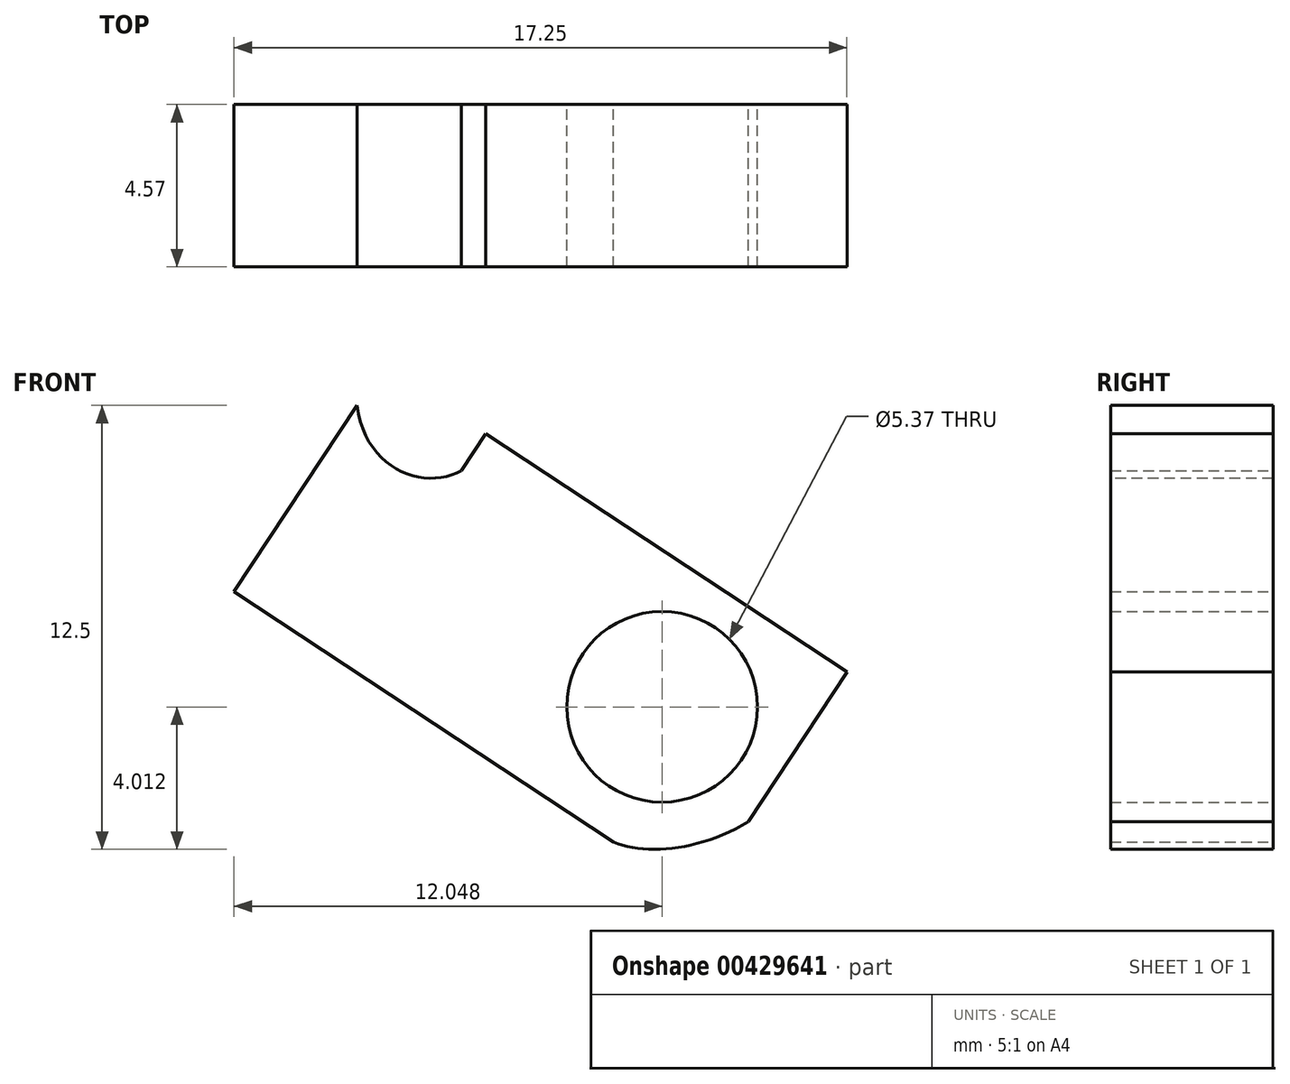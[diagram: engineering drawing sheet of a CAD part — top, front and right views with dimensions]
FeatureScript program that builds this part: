
annotation { "Feature Type Name" : "Feature", "Feature Type Description" : "" }
export const myFeature = defineFeature(function(context is Context, id is Id, definition is map)
    precondition{}
    {
        {
            var Q0;
            Q0=qCreatedBy(makeId("Front.planeOp"),FACE);
            var sketch = newSketch(context, id + "F0", { "sketchPlane" : qUnion([Q0])});
            skPoint(sketch, "E0.startSnap0", {"position": v(28.1, -23.32) * mm});
            skLineSegment(sketch, "E1", {"start": v(28.1, -18.75) * mm, "end": v(17.93, -12.05) * mm});
            skLineSegment(sketch, "E2", {"start": v(17.93, -12.05) * mm, "end": v(17.24, -13.08) * mm});
            skLineSegment(sketch, "E3", {"start": v(10.84, -16.5) * mm, "end": v(14.3, -11.25) * mm});
            skFitSpline(sketch, "E4", {"points": [v(14.3, -11.25) * mm, v(17.24, -13.08) * mm], "startDerivative": vector(0.67, -5.5) * mm, "endDerivative": vector(3.03, 1.74) * mm});
            skCircle(sketch, "E5", {"center": v(22.89, -19.74) * mm, "radius": 2.68 * mm});
            skFitSpline(sketch, "E6", {"points": [v(21.51, -23.54) * mm, v(25.31, -22.97) * mm], "startDerivative": vector(2.85, -1.15) * mm, "endDerivative": vector(4.08, 2.47) * mm});
            skLineSegment(sketch, "E7", {"start": v(25.31, -22.97) * mm, "end": v(28.1, -18.75) * mm});
            skLineSegment(sketch, "E8", {"start": v(21.51, -23.54) * mm, "end": v(10.84, -16.5) * mm});
            skSolve(sketch);
        }
        {
            var Q0;
            Q0=makeQuery(id+"F0.imprint","IMPRINT",FACE,{"disambiguationData":[TD([[makeQuery(id+"F0.imprint","IMPRINT",EDGE,{"derivedFrom":sQuery(id+"F0.wireOp",EDGE,"E1")}),1.0]])]});
            extrude(context, id + "F1", {"entities" : qUnion([Q0]), "depth" : 4.57 * mm});
        }
    });
